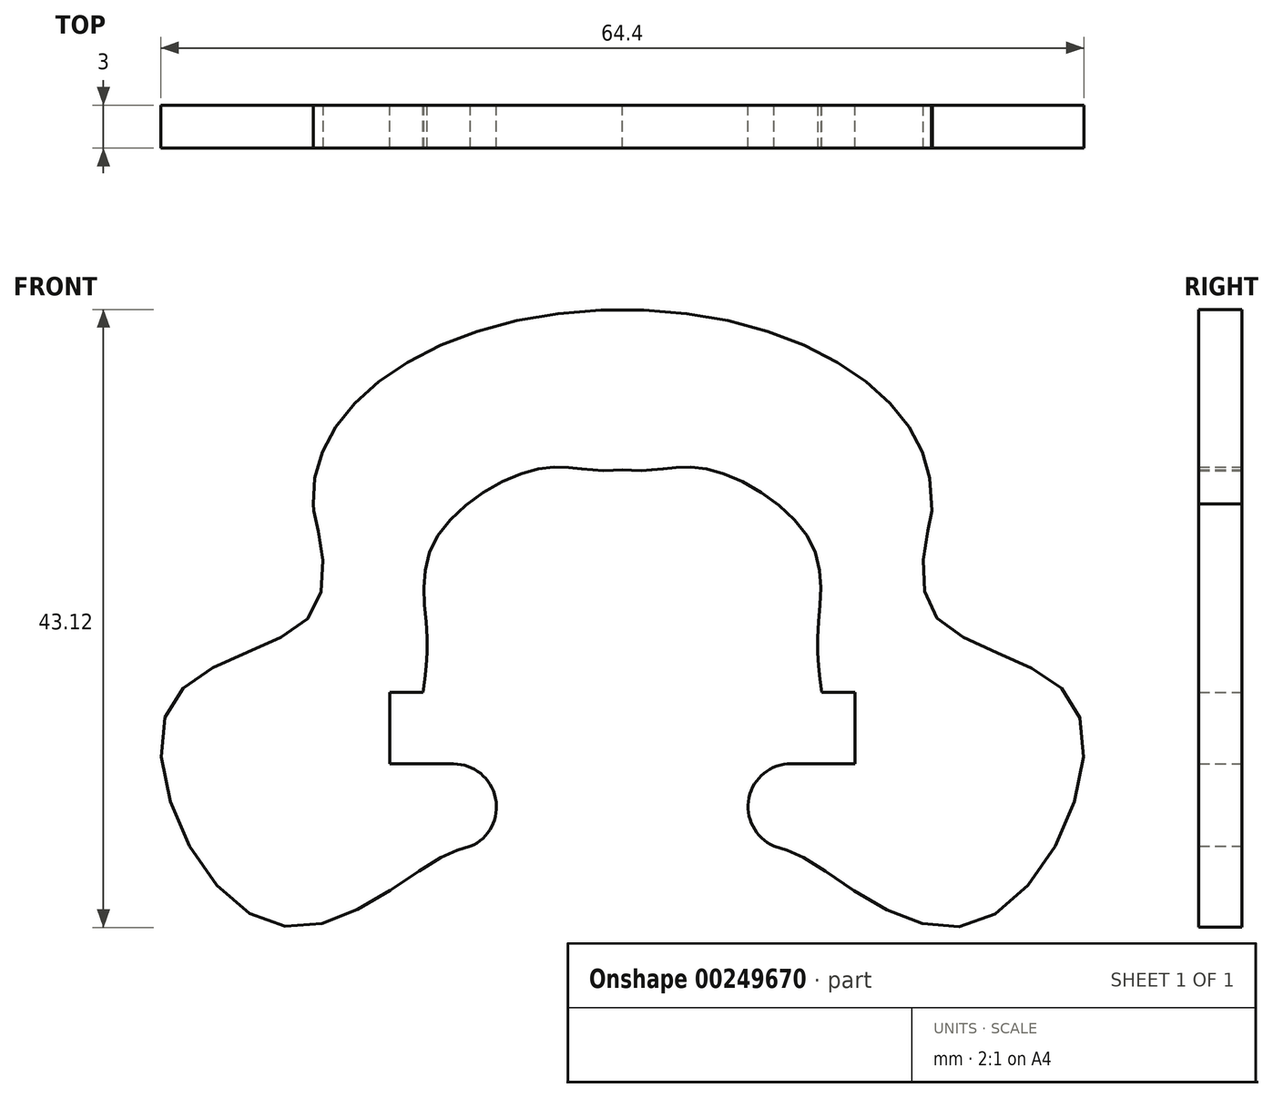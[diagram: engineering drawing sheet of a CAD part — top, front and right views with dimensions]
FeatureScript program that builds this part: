
annotation { "Feature Type Name" : "Feature", "Feature Type Description" : "" }
export const myFeature = defineFeature(function(context is Context, id is Id, definition is map)
    precondition{}
    {
        {
            var Q0;
            Q0=qCreatedBy(makeId("Front.planeOp"),FACE);
            var sketch = newSketch(context, id + "F0", { "sketchPlane" : qUnion([Q0])});
            skLineSegment(sketch, "E0", {"start": v(-16.22, -11.74) * mm, "end": v(-16.22, -6.74) * mm});
            skFitSpline(sketch, "E1", {"points": [v(-13.92, -6.74) * mm, v(-13.64, -2.66) * mm, v(-13.2, 3.6) * mm, v(-6.22, 8.76) * mm, v(-2.06, 8.77) * mm, v(0, 8.77) * mm]});
            skFitSpline(sketch, "E2", {"points": [v(13.91, -6.74) * mm, v(13.63, -2.66) * mm, v(13.2, 3.6) * mm, v(6.22, 8.76) * mm, v(2.06, 8.77) * mm, v(0, 8.77) * mm]});
            skLineSegment(sketch, "E3", {"start": v(16.21, -11.74) * mm, "end": v(16.21, -6.74) * mm});
            skLineSegment(sketch, "E4", {"start": v(16.21, -6.74) * mm, "end": v(13.91, -6.74) * mm});
            skLineSegment(sketch, "E5", {"start": v(-13.92, -6.74) * mm, "end": v(-16.22, -6.74) * mm});
            skEllipticalArc(sketch, "E6", {});
            skLineSegment(sketch, "E7", {"start": v(-16.22, -11.74) * mm, "end": v(-11.78, -11.74) * mm});
            skFitSpline(sketch, "E8", {"points": [v(-21.55, 6.39) * mm, v(-21.53, 6.02) * mm, v(-21.56, -1.08) * mm, v(-31.63, -7.76) * mm, v(-24.74, -22.8) * mm, v(-13.35, -18.68) * mm, v(-10.6, -17.5) * mm]});
            skArc(sketch, "E9", {"start": v(-10.6, -17.5) * mm, "mid": v(-8.84, -14.13) * mm, "end": v(-11.78, -11.74) * mm});
            skLineSegment(sketch, "E10", {"start": v(16.21, -11.74) * mm, "end": v(11.78, -11.72) * mm});
            skFitSpline(sketch, "E11", {"points": [v(21.55, 6.39) * mm, v(21.6, 6) * mm, v(21.6, -1.1) * mm, v(31.64, -7.82) * mm, v(24.69, -22.84) * mm, v(13.31, -18.67) * mm, v(10.57, -17.47) * mm]});
            skArc(sketch, "E12", {"start": v(11.78, -11.72) * mm, "mid": v(8.83, -14.1) * mm, "end": v(10.57, -17.47) * mm});
            const initialGuessF0  = {"E6": [-1.8650000001798617e-06, 0.006850431000000072, 21.563762, 0, 0.021563762, 0.013119126, 6.247711, 9.460252]};
            skSetInitialGuess(sketch, initialGuessF0);
            skSolve(sketch);
        }
        {
            var Q0;
            Q0 = qSketchRegion(id + "F0", true);
            extrude(context, id + "F1", {"entities" : qUnion([Q0]), "depth" : 3 * mm});
        }
    });
